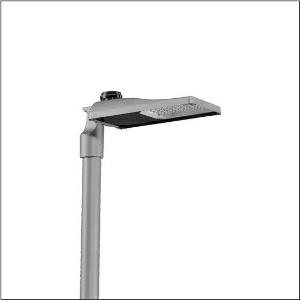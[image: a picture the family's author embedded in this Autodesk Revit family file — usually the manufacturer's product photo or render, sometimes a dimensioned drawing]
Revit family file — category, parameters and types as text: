
# Revit family: streetlight_sl_31_mini___st1_0a_5xh2d35n08ga_ac29
name_source: partatom
category: Lighting Fixtures
units: mm (PartAtom-declared; Revit-internal decimal feet)

## family parameters
Cut with Voids When Loaded = No
Host = Face
Light Source = No
Part Type = Normal
Room Calculation Point = No
Round Connector Dimension = Use Diameter
Shared = No

## types (1)
- --- (1 x LED, 5710 lm, 37.3 W, 3000K)
    Apparent Load = 37 VA
    CIE Flux Codes = 37 72 97 100 100
    Color Rendering = 70
    Color Temperature = 3000K
    Default Elevation = 1800 mm
    Description = Streetlight SL 31 mini NEMA (7pin), Desk-Remote mast luminaire for post-top, side-entry; light control with lens of PMMA; light distribution: ST1.0a, direct asymmetric distribution, for standard-compliant lighting for roads and squares; LED: luminous flux: 5.710lm, light colour: 730, colour temperature: 3000K; luminous efficacy: 153,1lm/W; control: pre-setting: linear dimming characteristic, flexible luminous flux parameterisation, time-dependent luminous flux control, constant luminous flux control, intelligent temperature release in ECG and LED module, overheat protection; luminaire housing, of diecast aluminium, Siteco® metallic grey (DB 702S), corrosivity category C5 high according to DIN EN ISO 12944; cover of toughened safety glass, transparent, mast flange of diecast aluminium, Siteco® metallic grey (DB 702S), spigot size: 76/60mm, mast flange included unmounted; with cable H07RN-F 3x 1.5mm², cable length: 6,5m, connection cable pre-assembled; mains connection: 220..240V, AC, 50/60Hz; power consumption (at start of service life): 37,3W / (at end of service life): 38,7W / (with reduced operation 50%): 17,5W; protection rating (complete): IP66; insulation class (complete): insulation class I (protective earthing); impact resistance: IK10; certification: CE, ENEC, ENEC+, VDE, UKCA; permissible operating ambient temperature for outdoor applications: -40..+50°C; packaging unit: 1 piece

Light Distribution: ST1.0a
    Height = 76 mm
    Lamp = 1 x LED
    Lamp Light Flux = 5710 lm
    Lamp Power = 37.3 W
    Lamp count = 1
    Length = 547 mm
    Luminous efficacy = 153 lm/W
    Manufacturer = Siteco
    ModVariant = No
    Model = 5XH2D35N08GA
    Number of Poles = 1
    OnlyDefault = Yes
    Power Factor = 1
    Product Name = Streetlight SL 31 mini | ST1.0a
    Product group = mast luminaire | pylon top
    ProductGroupID = 6100
    Protection Class = Protection class I
    Protection Degree = IP 66
    RLX_Detail_Level = 1
    RLX_Emergency_Light_Flux = 0 lm
    RLX_Emergency_Type = 0
    RLX_Emergency_Type_DB = No
    RlxData = <blob elided: 40121 chars, md5=781e74da>
    Socket = socket
    Standby Power = 0 W
    System Light Flux = 5710 lm
    System Power = 37 W
    Type Comments = factory setting: luminous flux: 100 % | dim-lin: 254 | 386 mA
    Type Image = l_1300322.jpg
    URL = http://relux.com
    VarID = @adj_054624
    Voltage = 0 V
    Weight = 0.00 kg
    Width = 265 mm

## geometry (parser evidence)
native form markers: Blend x4, Sweep x9
no freeform markers — native parametric forms only
